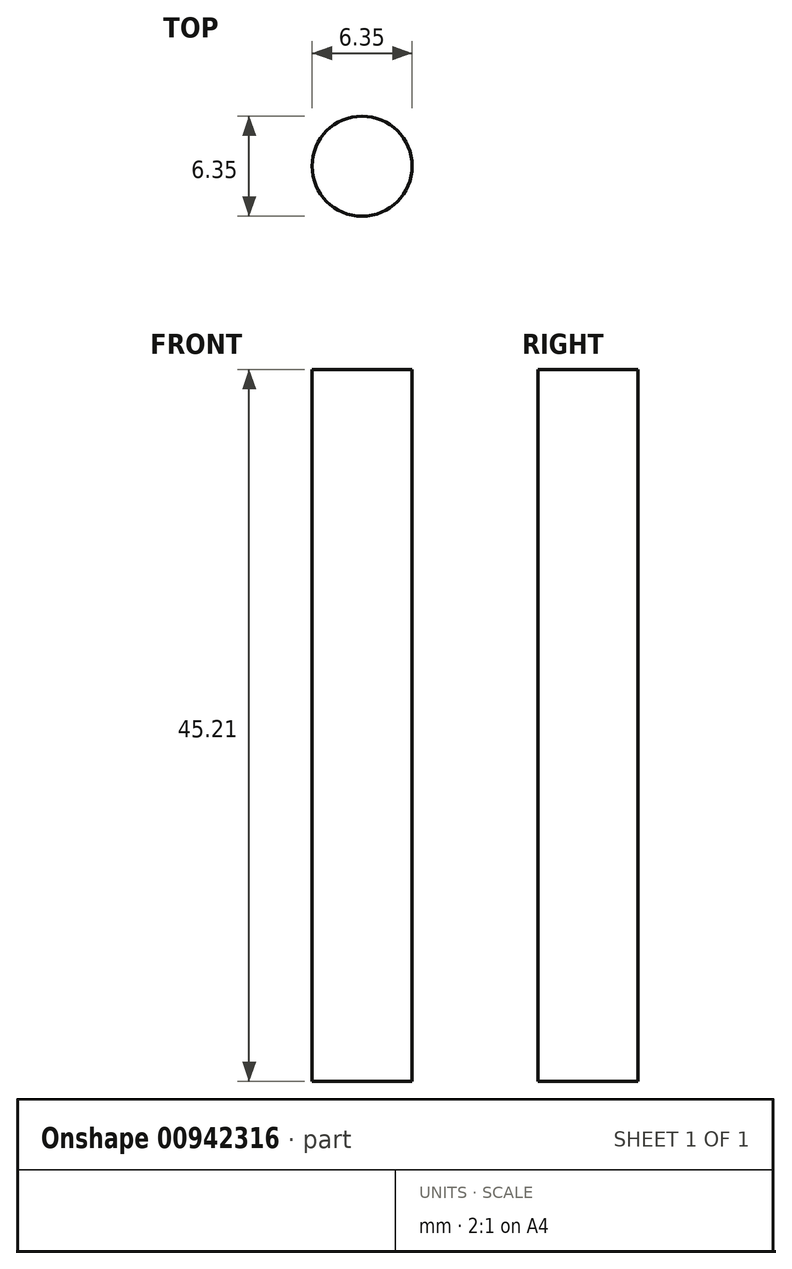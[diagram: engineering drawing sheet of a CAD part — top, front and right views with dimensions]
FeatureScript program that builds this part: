
annotation { "Feature Type Name" : "Feature", "Feature Type Description" : "" }
export const myFeature = defineFeature(function(context is Context, id is Id, definition is map)
    precondition{}
    {
        {
            var Q0;
            Q0=qCreatedBy(makeId("Top.planeOp"),FACE);
            var sketch = newSketch(context, id + "F0", { "sketchPlane" : qUnion([Q0])});
            skCircle(sketch, "E0", {"center": v(-46.47, 25.6) * mm, "radius": 3.18 * mm});
            skSolve(sketch);
        }
        {
            var Q0;
            Q0 = qSketchRegion(id + "F0", true);
            extrude(context, id + "F1", {"entities" : qUnion([Q0]), "depth" : 45.2 * mm, "offsetDistance" : 25.4 * mm});
        }
    });
